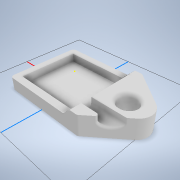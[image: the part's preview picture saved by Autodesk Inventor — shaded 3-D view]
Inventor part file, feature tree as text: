
AUTODESK INVENTOR PART (.ipt)
format: ipt  version: 2021 (Build 250183000, 183)  size: 239,616 bytes
history: native  units: mm
features: sketch x5, extrude x4, fillet x3, projected_geometry x2, chamfer x1
ambient origin geometry x8: Origin, YZ Plane, XZ Plane, XY Plane, X Axis, Y Axis, Z Axis, Center Point
bodies: Solid1 (feature_tree)
feature tree (15):
  extrude  "Extrusion1"  Depth=20.0mm
  extrude  "Extrusion2"  Depth=4.0mm
  sketch  "Sketch3"  dims[d4=2.0mm d5=6.0mm d6=19.0mm]
  extrude  "Extrusion3"  Depth=19.0mm
  fillet  "Fillet1"  Radius=19.0mm
  extrude  "Extrusion5"  Depth=4.4mm TaperAngle=0.0deg
  chamfer  "Chamfer1"  Distance=1.0mm
  fillet  "Fillet3"  Radius=2.8mm
  fillet  "Fillet4"  Radius=1.6mm
  sketch  "Sketch1"  dims[d0=23.0mm d1=20.0mm]
  sketch  "Sketch2"  dims[d2=5.0mm d3=4.0mm]
  projected_geometry  "Projected Loop1"
  sketch  "Sketch4"  dims[d7=16.0mm d8=4.4mm d9=0.0mm d10=1.0mm d11=0.0mm d12=2.8mm d13=1.6mm]
  sketch  "Sketch6"  dims[d14=1.0mm d16=2.8mm d17=0.0mm d18=0.0mm d23=1.0mm d24=2.0mm d25=0.0mm d26=2.0mm d27=2.0mm d28=45.0deg d30=0.5mm d31=0.5mm]
  projected_geometry  "Projected Loop3"
